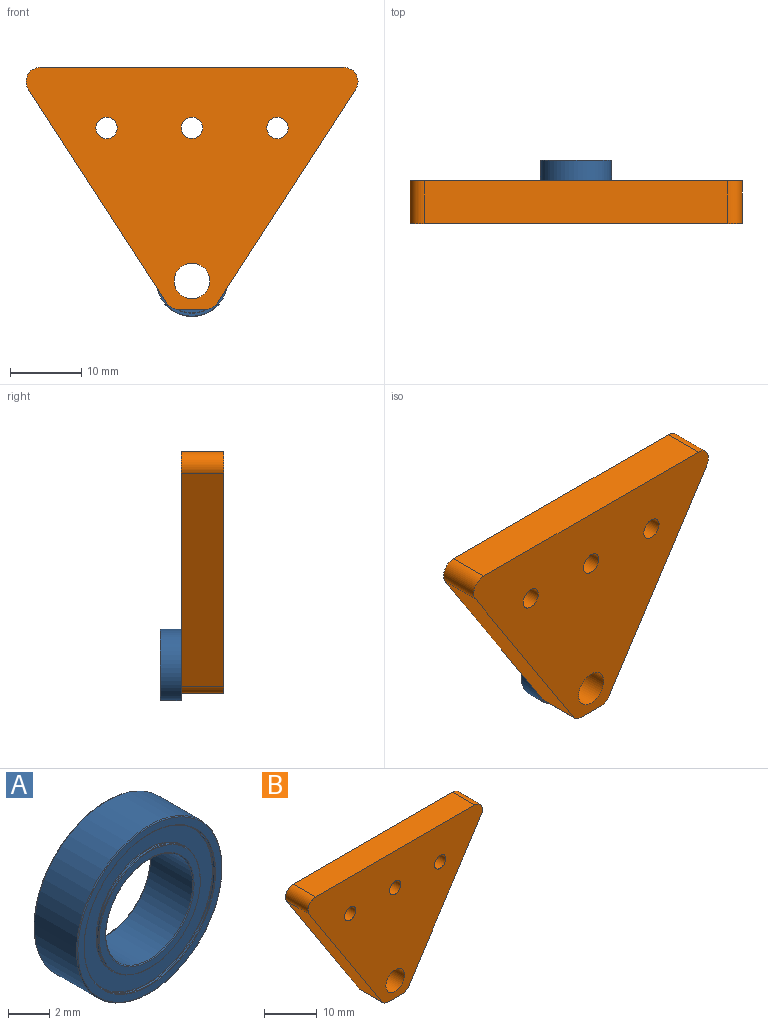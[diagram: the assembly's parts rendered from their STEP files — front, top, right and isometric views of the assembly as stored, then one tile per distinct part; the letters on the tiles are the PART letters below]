
ASSEMBLY  parts=2 mates=1
PART A: 24 faces, bbox 10.8x3x10.8 mm
  f0: plane 8.94x8.94mm, normal (0,-1,0), area 23.6mm2, adj f1,f23
  f1: torus R=3.53mm, axis (0,-1,0), area 1mm2, adj f0,f2
  f2: cylinder r=3.5mm len=7mm, axis (0,-1,0), area 2.3mm2, adj f1,f3
  f3: torus R=3.47mm, axis (0,-1,0), area 1mm2, adj f2,f4
  f4: plane 6.94x6.94mm, normal (0,-1,0), area 8.6mm2, adj f3,f5
  f5: torus R=3.05mm, axis (0,-1,0), area 1.5mm2, adj f4,f6
  f6: cylinder r=3mm len=6mm, axis (0,-1,0), area 54.7mm2, adj f5,f7
  f7: torus R=3.05mm, axis (0,-1,0), area 1.5mm2, adj f6,f8
  f8: plane 6.94x6.94mm, normal (0,1,0), area 8.6mm2, adj f7,f9
  f9: torus R=3.47mm, axis (0,-1,0), area 1mm2, adj f8,f10
  f10: cylinder r=3.5mm len=7mm, axis (0,-1,0), area 2.3mm2, adj f9,f11
  f11: torus R=3.53mm, axis (0,-1,0), area 1mm2, adj f10,f12
  f12: plane 8.94x8.94mm, normal (0,1,0), area 23.6mm2, adj f11,f13
  f13: torus R=4.47mm, axis (0,-1,0), area 1.3mm2, adj f12,f14
  f14: cylinder r=4.5mm len=9mm, axis (0,-1,0), area 3mm2, adj f13,f15
  f15: torus R=4.53mm, axis (0,-1,0), area 1.3mm2, adj f14,f16
  f16: plane 9.9x9.9mm, normal (0,1,0), area 12.5mm2, adj f15,f17
  f17: torus R=4.95mm, axis (0,-1,0), area 2.5mm2, adj f16,f18
  f18: cylinder r=5mm len=10mm, axis (0,-1,0), area 91.1mm2, adj f17,f19
  f19: torus R=4.95mm, axis (0,-1,0), area 2.5mm2, adj f18,f20
  f20: plane 9.9x9.9mm, normal (0,-1,0), area 12.5mm2, adj f19,f21
  f21: torus R=4.53mm, axis (0,-1,0), area 1.3mm2, adj f20,f22
  f22: cylinder r=4.5mm len=9mm, axis (0,-1,0), area 3mm2, adj f21,f23
  f23: torus R=4.47mm, axis (0,-1,0), area 1.3mm2, adj f0,f22
PART B: 14 faces, bbox 46.6x6x34 mm
  f0: plane 6x3.82mm, normal (0,0,-1), area 22.9mm2, adj f1,f10,f12,f13
  f1: cylinder r=2mm len=6mm, axis (0,1,0), area 12mm2, adj f0,f2,f12,f13
  f2: plane 30x19.41mm, normal (0.84,0,-0.54), area 214.4mm2, adj f1,f3,f12,f13
  f3: cylinder r=2mm len=6mm, axis (0,1,0), area 25.7mm2, adj f2,f4,f12,f13
  f4: plane 42.65x6mm, normal (0,0,1), area 255.9mm2, adj f3,f5,f12,f13
  f5: cylinder r=2mm len=6mm, axis (0,1,0), area 25.7mm2, adj f4,f6,f12,f13
  f6: plane 30x19.41mm, normal (-0.84,0,-0.54), area 214.4mm2, adj f5,f10,f12,f13
  f7: cylinder r=1.5mm len=6mm, axis (0,1,0), area 56.5mm2, adj f12,f13
  f8: cylinder r=1.5mm len=6mm, axis (0,1,0), area 56.5mm2, adj f12,f13
  f9: cylinder r=2.5mm len=6mm, axis (0,1,0), area 94.2mm2, adj f12,f13
  f10: cylinder r=2mm len=6mm, axis (0,1,0), area 12mm2, adj f0,f6,f12,f13
  f11: cylinder r=1.5mm len=6mm, axis (0,1,0), area 56.5mm2, adj f12,f13
  f12: plane 46.65x34mm, normal (0,-1,0), area 904.7mm2, adj f0,f1,f2,f3,f4,f5,f6,f7
  f13: plane 46.65x34mm, normal (0,1,0), area 904.7mm2, adj f0,f1,f2,f3,f4,f5,f6,f7
PLACE A t=(-4.94,2.52,-11.5)mm
PLACE B t=(-4.94,1.07,-11.5)mm
MATE cylindrical A.f1 <-> B.f9  axis (0,-1,0) through (-4.94,1.07,-11.5)mm
